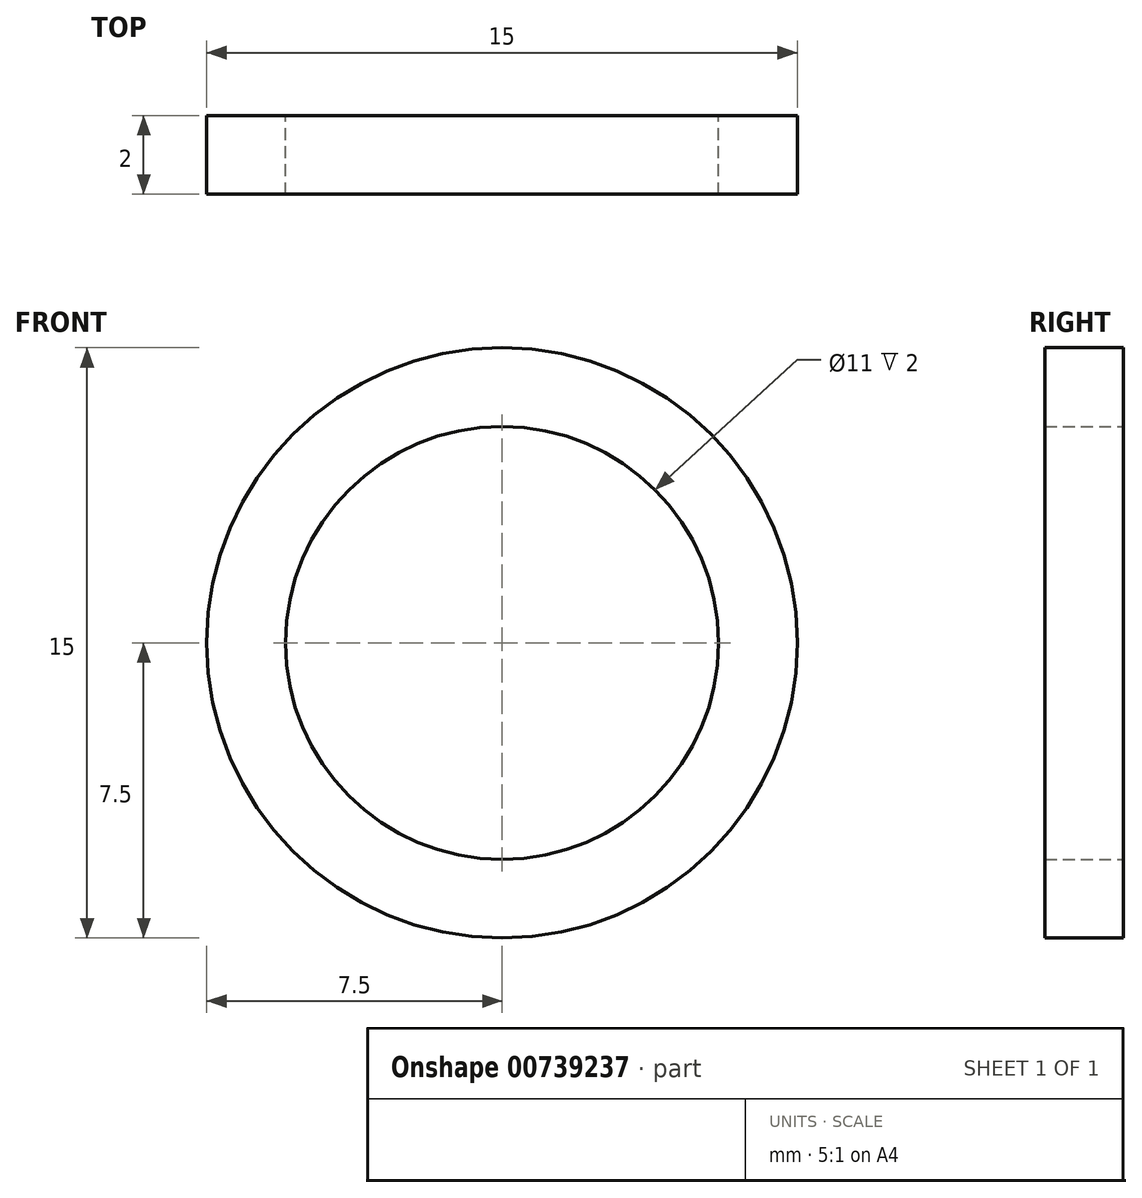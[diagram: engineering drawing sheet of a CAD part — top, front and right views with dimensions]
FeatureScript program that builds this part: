
annotation { "Feature Type Name" : "Feature", "Feature Type Description" : "" }
export const myFeature = defineFeature(function(context is Context, id is Id, definition is map)
    precondition{}
    {
        {
            var Q0;
            Q0=qCreatedBy(makeId("Front.planeOp"),FACE);
            var sketch = newSketch(context, id + "F0", { "sketchPlane" : qUnion([Q0])});
            skCircle(sketch, "E0", {"center": v(0, 0) * mm, "radius": 7.5 * mm});
            skCircle(sketch, "E1", {"center": v(0, 0) * mm, "radius": 5.5 * mm});
            skSolve(sketch);
        }
        {
            var Q0;
            Q0 = qSketchRegion(id + "F0", true);
            extrude(context, id + "F1", {"entities" : qUnion([Q0]), "depth" : 2 * mm, "offsetDistance" : 25.4 * mm});
        }
    });
